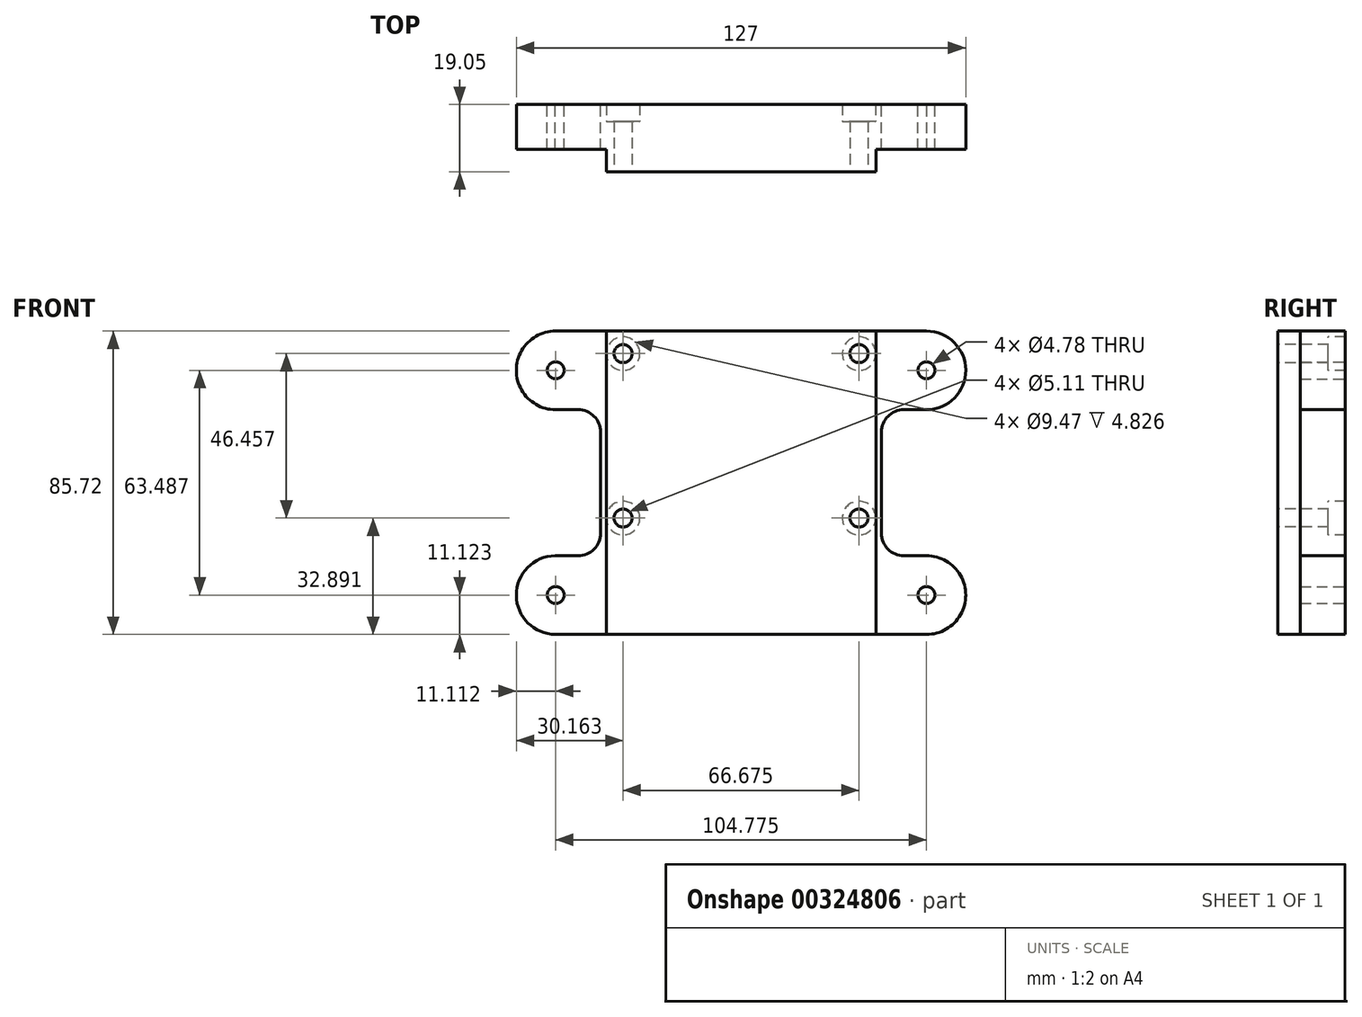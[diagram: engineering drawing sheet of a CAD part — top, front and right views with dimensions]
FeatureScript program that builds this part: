
annotation { "Feature Type Name" : "Feature", "Feature Type Description" : "" }
export const myFeature = defineFeature(function(context is Context, id is Id, definition is map)
    precondition{}
    {
        {
            var Q0;
            Q0=qCreatedBy(makeId("Front.planeOp"),FACE);
            var sketch = newSketch(context, id + "F0", { "sketchPlane" : qUnion([Q0])});
            skPoint(sketch, "E0.middle", {"position": v(0, 0) * mm});
            skArc(sketch, "E1", {"start": v(-52.39, 42.86) * mm, "mid": v(-63.5, 31.75) * mm, "end": v(-52.39, 20.64) * mm});
            skArc(sketch, "E2", {"start": v(52.53, 20.64) * mm, "mid": v(63.5, 31.82) * mm, "end": v(52.39, 42.86) * mm});
            skArc(sketch, "E3", {"start": v(52.39, -42.86) * mm, "mid": v(63.5, -31.75) * mm, "end": v(52.39, -20.64) * mm});
            skArc(sketch, "E4", {"start": v(-52.53, -20.64) * mm, "mid": v(-63.5, -31.82) * mm, "end": v(-52.39, -42.86) * mm});
            skLineSegment(sketch, "E5", {"start": v(-52.39, 42.86) * mm, "end": v(52.39, 42.86) * mm});
            skLineSegment(sketch, "E6", {"start": v(-52.39, -42.86) * mm, "end": v(52.39, -42.86) * mm});
            skLineSegment(sketch, "E7", {"start": v(-52.39, 20.64) * mm, "end": v(-39.69, 20.64) * mm});
            skLineSegment(sketch, "E8", {"start": v(-52.53, -20.64) * mm, "end": v(-39.69, -20.64) * mm});
            skLineSegment(sketch, "E9", {"start": v(-39.69, 20.64) * mm, "end": v(-39.69, -20.64) * mm});
            skLineSegment(sketch, "E10", {"start": v(39.69, 20.64) * mm, "end": v(39.69, -20.64) * mm});
            skLineSegment(sketch, "E11.trimOffspring", {"start": v(39.69, -20.64) * mm, "end": v(52.39, -20.64) * mm});
            skLineSegment(sketch, "E12.trimOffspring", {"start": v(39.69, 20.64) * mm, "end": v(52.53, 20.64) * mm});
            skSolve(sketch);
        }
        {
            var Q0;
            Q0=makeQuery(id+"F0.imprint","IMPRINT",FACE,{"disambiguationData":[TD([[makeQuery(id+"F0.imprint","IMPRINT",EDGE,{"derivedFrom":sQuery(id+"F0.wireOp",EDGE,"E1")}),1.0]])]});
            extrude(context, id + "F1", {"entities" : qUnion([Q0]), "depth" : 12.7 * mm});
        }
        {
            var Q0;
            Q0=makeQuery(id+"F1.opExtrude","SWEPT_EDGE",EDGE,{"disambiguationData":[OSD([sQuery(id+"F0.wireOp",EDGE,"E7"),sQuery(id+"F0.wireOp",EDGE,"E9")])]});
            var Q1;
            Q1=makeQuery(id+"F1.opExtrude","SWEPT_EDGE",EDGE,{"disambiguationData":[OSD([sQuery(id+"F0.wireOp",EDGE,"E8"),sQuery(id+"F0.wireOp",EDGE,"E9")])]});
            var Q2;
            Q2=makeQuery(id+"F1.opExtrude","SWEPT_EDGE",EDGE,{"disambiguationData":[OSD([sQuery(id+"F0.wireOp",EDGE,"E10"),sQuery(id+"F0.wireOp",EDGE,"E12.trimOffspring")])]});
            var Q3;
            Q3=makeQuery(id+"F1.opExtrude","SWEPT_EDGE",EDGE,{"disambiguationData":[OSD([sQuery(id+"F0.wireOp",EDGE,"E10"),sQuery(id+"F0.wireOp",EDGE,"E11.trimOffspring")])]});
            fillet(context, id + "F2", {"entities" : qUnion([Q0, Q1, Q2, Q3]), "radius" : 6.35 * mm, "tangentPropagation" : true, "allowEdgeOverflow" : false});
        }
        {
            var Q0;
            Q0=makeQuery(id+"F1.opExtrude","CAP_FACE",FACE,{"disambiguationData":[OSD([sQuery(id+"F0.wireOp",EDGE,"E1"),sQuery(id+"F0.wireOp",EDGE,"E2"),sQuery(id+"F0.wireOp",EDGE,"E3"),sQuery(id+"F0.wireOp",EDGE,"E4"),sQuery(id+"F0.wireOp",EDGE,"E5"),sQuery(id+"F0.wireOp",EDGE,"E6"),sQuery(id+"F0.wireOp",EDGE,"E7"),sQuery(id+"F0.wireOp",EDGE,"E8"),sQuery(id+"F0.wireOp",EDGE,"E9"),sQuery(id+"F0.wireOp",EDGE,"E10"),sQuery(id+"F0.wireOp",EDGE,"E11.trimOffspring"),sQuery(id+"F0.wireOp",EDGE,"E12.trimOffspring")])],"isStart":false});
            var sketch = newSketch(context, id + "F3", { "sketchPlane" : qUnion([Q0])});
            skLineSegment(sketch, "E13.bottom", {"start": v(38.1, -42.86) * mm, "end": v(-38.1, -42.86) * mm});
            skLineSegment(sketch, "E13.top", {"start": v(38.1, 42.86) * mm, "end": v(-38.1, 42.86) * mm});
            skLineSegment(sketch, "E13.left", {"start": v(38.1, -42.86) * mm, "end": v(38.1, 42.86) * mm});
            skLineSegment(sketch, "E13.right", {"start": v(-38.1, -42.86) * mm, "end": v(-38.1, 42.86) * mm});
            skPoint(sketch, "E13.middle", {"position": v(0, 0) * mm});
            skSolve(sketch);
        }
        {
            var Q0;
            {var subQ8=sQuery(id+"F3.wireOp",EDGE,"E13.bottom");Q0=makeQuery(id+"F3.imprint","IMPRINT",FACE,{"disambiguationData":[TD([[makeQuery(id+"F3.imprint","IMPRINT",EDGE,{"derivedFrom":subQ8}),1.0]])]});}
            var Q1;
            {var subQ0=sQuery(id+"F3.wireOp",EDGE,"E13.left");var subQ3=makeQuery(id+"F1.opExtrude","CAP_EDGE",EDGE,{"disambiguationData":[OSD([sQuery(id+"F0.wireOp",EDGE,"E5")])],"isStart":false});var subQ4=makeQuery(id+"F3.imprint","INTERSECT",VERTEX,{"derivedFrom":[subQ3,subQ0]});Q1=makeQuery(id+"F3.imprint","IMPRINT",FACE,{"disambiguationData":[TD([[makeQuery(id+"F3.imprint","IMPRINT",EDGE,{"disambiguationData":[TD([[subQ4,1.0]])],"derivedFrom":subQ0}),1.0]])]});}
            extrude(context, id + "F4", {"entities" : qUnion([Q0, Q1]), "operationType" : NewBodyOperationType.ADD, "depth" : 6.35 * mm, "offsetDistance" : 25.4 * mm});
        }
        {
            var Q0;
            {var subQ0=sQuery(id+"F0.wireOp",EDGE,"E7");var subQ1=sQuery(id+"F0.wireOp",EDGE,"E5");var subQ2=sQuery(id+"F0.wireOp",EDGE,"E9");var subQ3=sQuery(id+"F0.wireOp",EDGE,"E1");Q0=makeQuery(id+"F4.boolean.opBoolean","SPLIT",FACE,{"disambiguationData":[TD([makeQuery(id+"F1.opExtrude","SWEPT_FACE",FACE,{"disambiguationData":[OSD([subQ3])]})])],"derivedFrom":makeQuery(id+"F1.opExtrude","CAP_FACE",FACE,{"disambiguationData":[OSD([subQ3,sQuery(id+"F0.wireOp",EDGE,"E2"),sQuery(id+"F0.wireOp",EDGE,"E3"),sQuery(id+"F0.wireOp",EDGE,"E4"),subQ1,sQuery(id+"F0.wireOp",EDGE,"E6"),subQ0,sQuery(id+"F0.wireOp",EDGE,"E8"),subQ2,sQuery(id+"F0.wireOp",EDGE,"E10"),sQuery(id+"F0.wireOp",EDGE,"E11.trimOffspring"),sQuery(id+"F0.wireOp",EDGE,"E12.trimOffspring")])],"isStart":false})});}
            var sketch = newSketch(context, id + "F5", { "sketchPlane" : qUnion([Q0])});
            skPoint(sketch, "E14", {"position": v(-52.39, 31.75) * mm});
            skPoint(sketch, "E15", {"position": v(-52.39, -31.74) * mm});
            skPoint(sketch, "E16", {"position": v(52.39, -31.74) * mm});
            skPoint(sketch, "E17", {"position": v(52.39, 31.75) * mm});
            skSolve(sketch);
        }
        {
            var Q0;
            Q0=sQuery(id+"F5.wireOp",VERTEX,"E14");
            var Q1;
            Q1=sQuery(id+"F5.wireOp",VERTEX,"E17");
            var Q2;
            Q2=sQuery(id+"F5.wireOp",VERTEX,"E16");
            var Q3;
            Q3=sQuery(id+"F5.wireOp",VERTEX,"E15");
            var Q4;
            Q4=makeQuery(id+"F1.opExtrude","SWEPT_BODY",BODY,{"disambiguationData":[OSD([sQuery(id+"F0.wireOp",EDGE,"E1"),sQuery(id+"F0.wireOp",EDGE,"E2"),sQuery(id+"F0.wireOp",EDGE,"E3"),sQuery(id+"F0.wireOp",EDGE,"E4"),sQuery(id+"F0.wireOp",EDGE,"E5"),sQuery(id+"F0.wireOp",EDGE,"E6"),sQuery(id+"F0.wireOp",EDGE,"E7"),sQuery(id+"F0.wireOp",EDGE,"E8"),sQuery(id+"F0.wireOp",EDGE,"E9"),sQuery(id+"F0.wireOp",EDGE,"E10"),sQuery(id+"F0.wireOp",EDGE,"E11.trimOffspring"),sQuery(id+"F0.wireOp",EDGE,"E12.trimOffspring")])]});
            hole(context, id + "F6", {"style" : HoleStyle.SIMPLE, "endStyle" : HoleEndStyle.THROUGH, "holeDiameter" : 4.78 * mm, "tappedDepth" : 12.7 * mm, "tapClearance" : 3, "locations" : qUnion([Q0, Q1, Q2, Q3]), "scope" : qUnion([Q4])});
        }
        {
            var Q0;
            Q0=makeQuery(id+"F1.opExtrude","CAP_FACE",FACE,{"disambiguationData":[OSD([sQuery(id+"F0.wireOp",EDGE,"E1"),sQuery(id+"F0.wireOp",EDGE,"E2"),sQuery(id+"F0.wireOp",EDGE,"E3"),sQuery(id+"F0.wireOp",EDGE,"E4"),sQuery(id+"F0.wireOp",EDGE,"E5"),sQuery(id+"F0.wireOp",EDGE,"E6"),sQuery(id+"F0.wireOp",EDGE,"E7"),sQuery(id+"F0.wireOp",EDGE,"E8"),sQuery(id+"F0.wireOp",EDGE,"E9"),sQuery(id+"F0.wireOp",EDGE,"E10"),sQuery(id+"F0.wireOp",EDGE,"E11.trimOffspring"),sQuery(id+"F0.wireOp",EDGE,"E12.trimOffspring")])],"isStart":true});
            var sketch = newSketch(context, id + "F7", { "sketchPlane" : qUnion([Q0])});
            skLineSegment(sketch, "E18", {"start": v(-70.03, 36.49) * mm, "end": v(68.32, 36.49) * mm, "construction": true});
            skLineSegment(sketch, "E19", {"start": v(-60.27, -9.97) * mm, "end": v(59.93, -9.97) * mm, "construction": true});
            skLineSegment(sketch, "E20", {"start": v(-33.34, 46.7) * mm, "end": v(-33.34, -48.68) * mm, "construction": true});
            skLineSegment(sketch, "E21", {"start": v(33.34, 48.06) * mm, "end": v(33.34, -48.85) * mm, "construction": true});
            skPoint(sketch, "E22", {"position": v(-33.34, 36.49) * mm});
            skPoint(sketch, "E23", {"position": v(33.34, 36.49) * mm});
            skPoint(sketch, "E24", {"position": v(33.34, -9.97) * mm});
            skPoint(sketch, "E25", {"position": v(-33.34, -9.97) * mm});
            skSolve(sketch);
        }
        {
            var Q0;
            Q0=sQuery(id+"F7.wireOp",VERTEX,"E22");
            var Q1;
            Q1=sQuery(id+"F7.wireOp",VERTEX,"E23");
            var Q2;
            Q2=sQuery(id+"F7.wireOp",VERTEX,"E24");
            var Q3;
            Q3=sQuery(id+"F7.wireOp",VERTEX,"E25");
            var Q4;
            Q4=makeQuery(id+"F1.opExtrude","SWEPT_BODY",BODY,{"disambiguationData":[OSD([sQuery(id+"F0.wireOp",EDGE,"E1"),sQuery(id+"F0.wireOp",EDGE,"E2"),sQuery(id+"F0.wireOp",EDGE,"E3"),sQuery(id+"F0.wireOp",EDGE,"E4"),sQuery(id+"F0.wireOp",EDGE,"E5"),sQuery(id+"F0.wireOp",EDGE,"E6"),sQuery(id+"F0.wireOp",EDGE,"E7"),sQuery(id+"F0.wireOp",EDGE,"E8"),sQuery(id+"F0.wireOp",EDGE,"E9"),sQuery(id+"F0.wireOp",EDGE,"E10"),sQuery(id+"F0.wireOp",EDGE,"E11.trimOffspring"),sQuery(id+"F0.wireOp",EDGE,"E12.trimOffspring")])]});
            hole(context, id + "F8", {"style" : HoleStyle.C_BORE, "endStyle" : HoleEndStyle.THROUGH, "holeDiameter" : 5.1 * mm, "cBoreDiameter" : 9.47 * mm, "cBoreDepth" : 4.83 * mm, "tappedDepth" : 12.7 * mm, "tapClearance" : 3, "locations" : qUnion([Q0, Q1, Q2, Q3]), "scope" : qUnion([Q4]), "majorDiameter" : 6.35 * mm});
        }
    });
